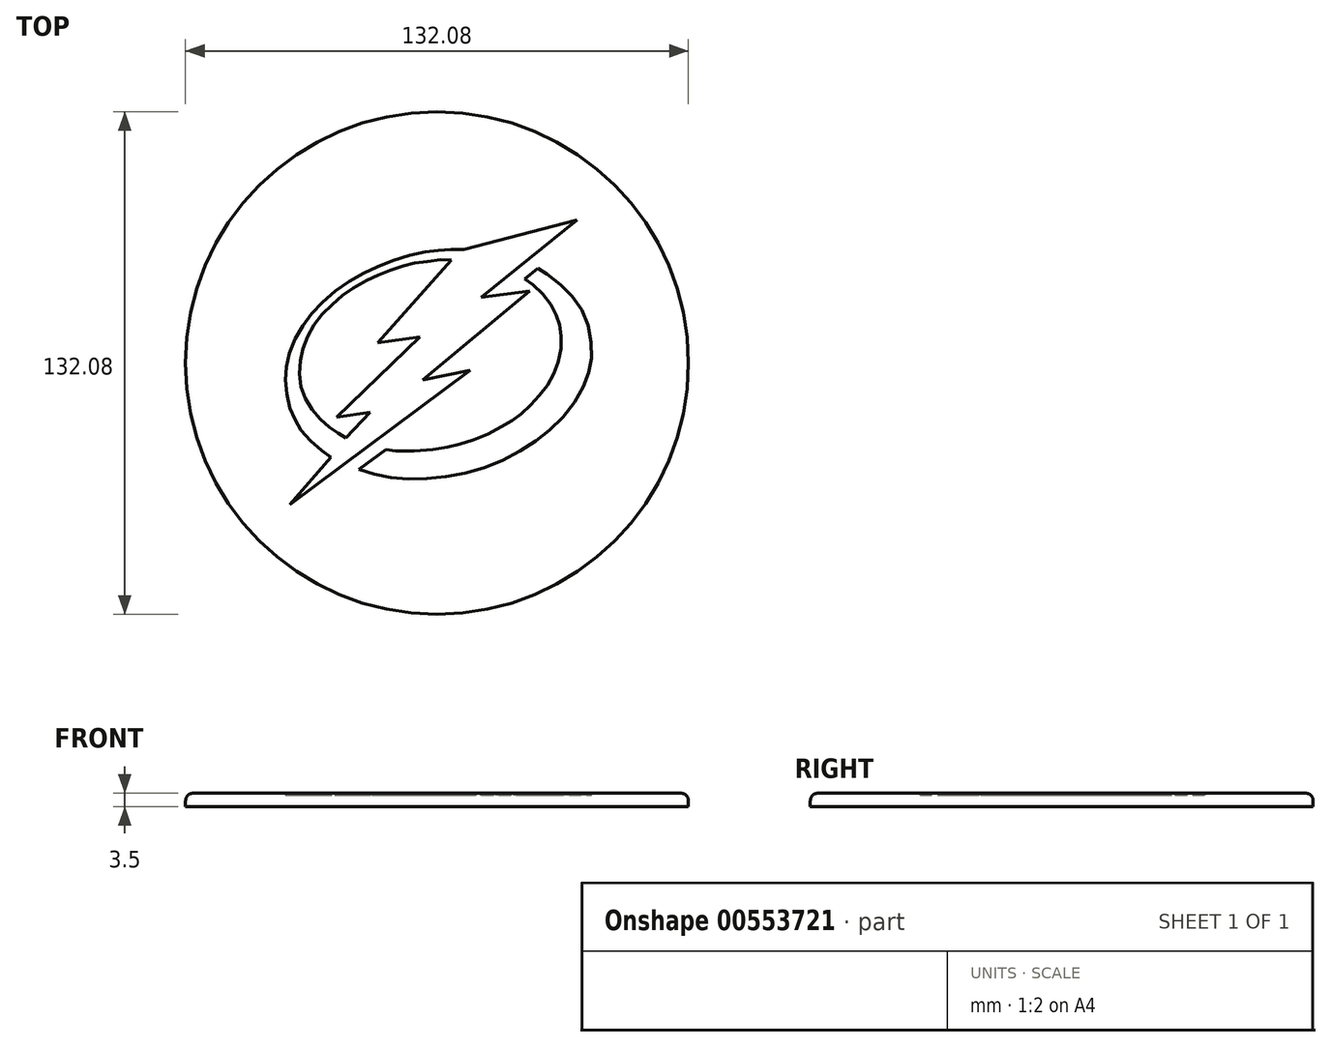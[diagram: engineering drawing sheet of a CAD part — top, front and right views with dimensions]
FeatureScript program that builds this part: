
annotation { "Feature Type Name" : "Feature", "Feature Type Description" : "" }
export const myFeature = defineFeature(function(context is Context, id is Id, definition is map)
    precondition{}
    {
        {
            var Q0;
            Q0=qCreatedBy(makeId("Top.planeOp"),FACE);
            var sketch = newSketch(context, id + "F0", { "sketchPlane" : qUnion([Q0])});
            skCircle(sketch, "E0", {"center": v(0, 0) * mm, "radius": 66.04 * mm});
            skSolve(sketch);
        }
        {
            var Q0;
            Q0 = qSketchRegion(id + "F0", true);
            extrude(context, id + "F1", {"entities" : qUnion([Q0]), "depth" : 3.5 * mm, "offsetDistance" : 25 * mm});
        }
        {
            var Q0;
            Q0=makeQuery(id+"F1.opExtrude","CAP_FACE",FACE,{"disambiguationData":[OSD([sQuery(id+"F0.wireOp",EDGE,"E0")])],"isStart":false});
            var sketch = newSketch(context, id + "F2", { "sketchPlane" : qUnion([Q0])});
            skLineSegment(sketch, "E1", {"start": v(0.13, 46.74) * mm, "end": v(0.13, -46.31) * mm, "construction": true});
            skLineSegment(sketch, "E2", {"start": v(-46.4, 0.22) * mm, "end": v(46.65, 0.22) * mm, "construction": true});
            skFitSpline(sketch, "E3", {"points": [v(3.74, 27.12) * mm, v(1.35, 27.16) * mm, v(-2, 26.78) * mm, v(-5.55, 26.3) * mm, v(-8.17, 25.66) * mm, v(-11.83, 24.55) * mm, v(-15.15, 23.27) * mm, v(-18.35, 21.75) * mm, v(-22.56, 19.42) * mm, v(-25.34, 17.34) * mm, v(-28.4, 14.58) * mm, v(-31.07, 11.71) * mm, v(-33.15, 8.6) * mm, v(-34.73, 5.33) * mm, v(-35.63, 1.93) * mm, v(-36.03, -0.8) * mm, v(-35.95, -4.84) * mm, v(-35.2, -7.75) * mm, v(-33.66, -11.05) * mm, v(-31.72, -13.64) * mm, v(-29.35, -15.97) * mm, v(-26.96, -17.76) * mm, v(-25.38, -18.77) * mm, v(-23.88, -19.68) * mm], "startDerivative": vector(-62.18, 3.4) * mm, "endDerivative": vector(47.74, -28.76) * mm});
            skLineSegment(sketch, "E4", {"start": v(-23.88, -19.68) * mm, "end": v(-17.62, -12.9) * mm});
            skLineSegment(sketch, "E5", {"start": v(-17.62, -12.9) * mm, "end": v(-26.33, -14.19) * mm});
            skLineSegment(sketch, "E6", {"start": v(-26.33, -14.19) * mm, "end": v(-4.5, 6.9) * mm});
            skLineSegment(sketch, "E7", {"start": v(-4.5, 6.9) * mm, "end": v(-15.5, 5.29) * mm});
            skLineSegment(sketch, "E8", {"start": v(-15.5, 5.29) * mm, "end": v(3.74, 27.12) * mm});
            skLineSegment(sketch, "E9", {"start": v(7.09, 29.8) * mm, "end": v(36.76, 37.63) * mm});
            skLineSegment(sketch, "E10", {"start": v(36.76, 37.63) * mm, "end": v(11.56, 17.32) * mm});
            skLineSegment(sketch, "E11", {"start": v(11.56, 17.32) * mm, "end": v(24.27, 18.88) * mm});
            skLineSegment(sketch, "E12", {"start": v(24.27, 18.88) * mm, "end": v(-3.72, -4.45) * mm});
            skLineSegment(sketch, "E13", {"start": v(-3.72, -4.45) * mm, "end": v(8.68, -1.9) * mm});
            skLineSegment(sketch, "E14", {"start": v(-38.65, -37.2) * mm, "end": v(-27.92, -24.73) * mm});
            skFitSpline(sketch, "E15", {"points": [v(-27.92, -24.73) * mm, v(-30.35, -22.94) * mm, v(-34.54, -19.09) * mm, v(-36.75, -15.79) * mm, v(-38.4, -12.35) * mm, v(-39.57, -7.5) * mm, v(-39.74, -2.9) * mm, v(-39.18, 1.3) * mm, v(-37.05, 6.7) * mm, v(-34.12, 11.45) * mm, v(-30.07, 16.03) * mm, v(-24.73, 20.4) * mm, v(-18.84, 23.83) * mm, v(-13.47, 26.26) * mm, v(-6.15, 28.6) * mm, v(-0.9, 29.47) * mm, v(2.87, 29.83) * mm, v(7.09, 29.8) * mm], "startDerivative": vector(-49.19, 34.53) * mm, "endDerivative": vector(80.85, -2.42) * mm});
            skFitSpline(sketch, "E16", {"points": [v(8.68, -1.9) * mm, v(-38.65, -37.2) * mm], "startDerivative": vector(-47.33, -35.29) * mm, "endDerivative": vector(-47.33, -35.29) * mm});
            skLineSegment(sketch, "E17", {"start": v(-13.34, -22.72) * mm, "end": v(-20.45, -27.98) * mm});
            skFitSpline(sketch, "E18", {"points": [v(-20.45, -27.98) * mm, v(-15.47, -29.4) * mm, v(-9.86, -30.39) * mm, v(-3.5, -30.42) * mm, v(3.77, -29.63) * mm, v(10.92, -27.98) * mm, v(18.11, -25.17) * mm, v(24.9, -21.18) * mm, v(29.69, -17.54) * mm, v(34.47, -12.49) * mm, v(38.03, -6.96) * mm, v(39.8, -2.57) * mm, v(40.55, 1.46) * mm, v(40.24, 6.76) * mm, v(38.9, 12.25) * mm, v(35.93, 16.95) * mm, v(32.41, 20.62) * mm, v(27.99, 23.98) * mm, v(26.45, 24.9) * mm], "startDerivative": vector(92.67, -28.29) * mm, "endDerivative": vector(-42.72, 23.17) * mm});
            skLineSegment(sketch, "E19", {"start": v(26.45, 24.9) * mm, "end": v(23.01, 22.12) * mm});
            skFitSpline(sketch, "E20", {"points": [v(23.01, 22.12) * mm, v(24.99, 20.7) * mm, v(28.13, 17.72) * mm, v(30.53, 14.25) * mm, v(31.82, 11.4) * mm, v(32.36, 8.91) * mm, v(32.62, 5.41) * mm, v(32.01, 0.93) * mm, v(30.65, -2.88) * mm, v(28.65, -6.38) * mm, v(25.76, -9.79) * mm, v(23.01, -12.56) * mm, v(20.31, -14.7) * mm, v(16.93, -16.72) * mm, v(12, -19.25) * mm, v(6.61, -21.16) * mm, v(2.74, -22.07) * mm, v(-2.97, -22.92) * mm, v(-11.38, -23.08) * mm, v(-13.34, -22.72) * mm], "startDerivative": vector(45.9, -30.9) * mm, "endDerivative": vector(-42.03, 11.54) * mm});
            skSolve(sketch);
        }
        {
            var Q0;
            Q0 = qSketchRegion(id + "F2", true);
            extrude(context, id + "F3", {"entities" : qUnion([Q0]), "operationType" : NewBodyOperationType.REMOVE, "oppositeDirection" : true, "depth" : .5 * mm, "offsetDistance" : 25 * mm});
        }
        {
            var Q0;
            Q0=makeQuery(id+"F1.opExtrude","CAP_EDGE",EDGE,{"disambiguationData":[OSD([sQuery(id+"F0.wireOp",EDGE,"E0")])],"isStart":false});
            fillet(context, id + "F4", {"entities" : qUnion([Q0]), "radius" : 2 * mm, "tangentPropagation" : true, "allowEdgeOverflow" : false});
        }
    });
